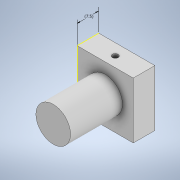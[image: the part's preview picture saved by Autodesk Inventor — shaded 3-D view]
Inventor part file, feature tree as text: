
AUTODESK INVENTOR PART (.ipt)
format: ipt  version: 2020 (Build 240168000, 168)  size: 126,464 bytes
history: native  units: in
note: dims shown in document units (in); Inventor stores cm internally (conversion verified against a paired STEP export)
features: sketch x4, extrude x3, projected_geometry x1
ambient origin geometry x8: Origin, YZ Plane, XZ Plane, XY Plane, X Axis, Y Axis, Z Axis, Center Point
bodies: Solid1 (feature_tree)
feature tree (8):
  extrude  "Extrusion1"  Depth=0.7677in
  sketch  "Sketch6"  dims[d2=0.2953in d3=0.0in d14=0.4724in]
  sketch  "Sketch7"  dims[d15=0.2953in d16=0.7087in d17=0.0in]
  extrude  "Extrusion4"  Depth=0.2953in
  extrude  "Extrusion5"  Depth=0.7087in TaperAngle=0.0deg
  sketch  "Sketch1"  dims[d0=0.7677in d1=0.7677in]
  projected_geometry  "Projected Loop4"
  sketch  "Sketch8"  dims[d18=0.1969in d19=0.0787in d20=0.7087in d21=0.0in]
